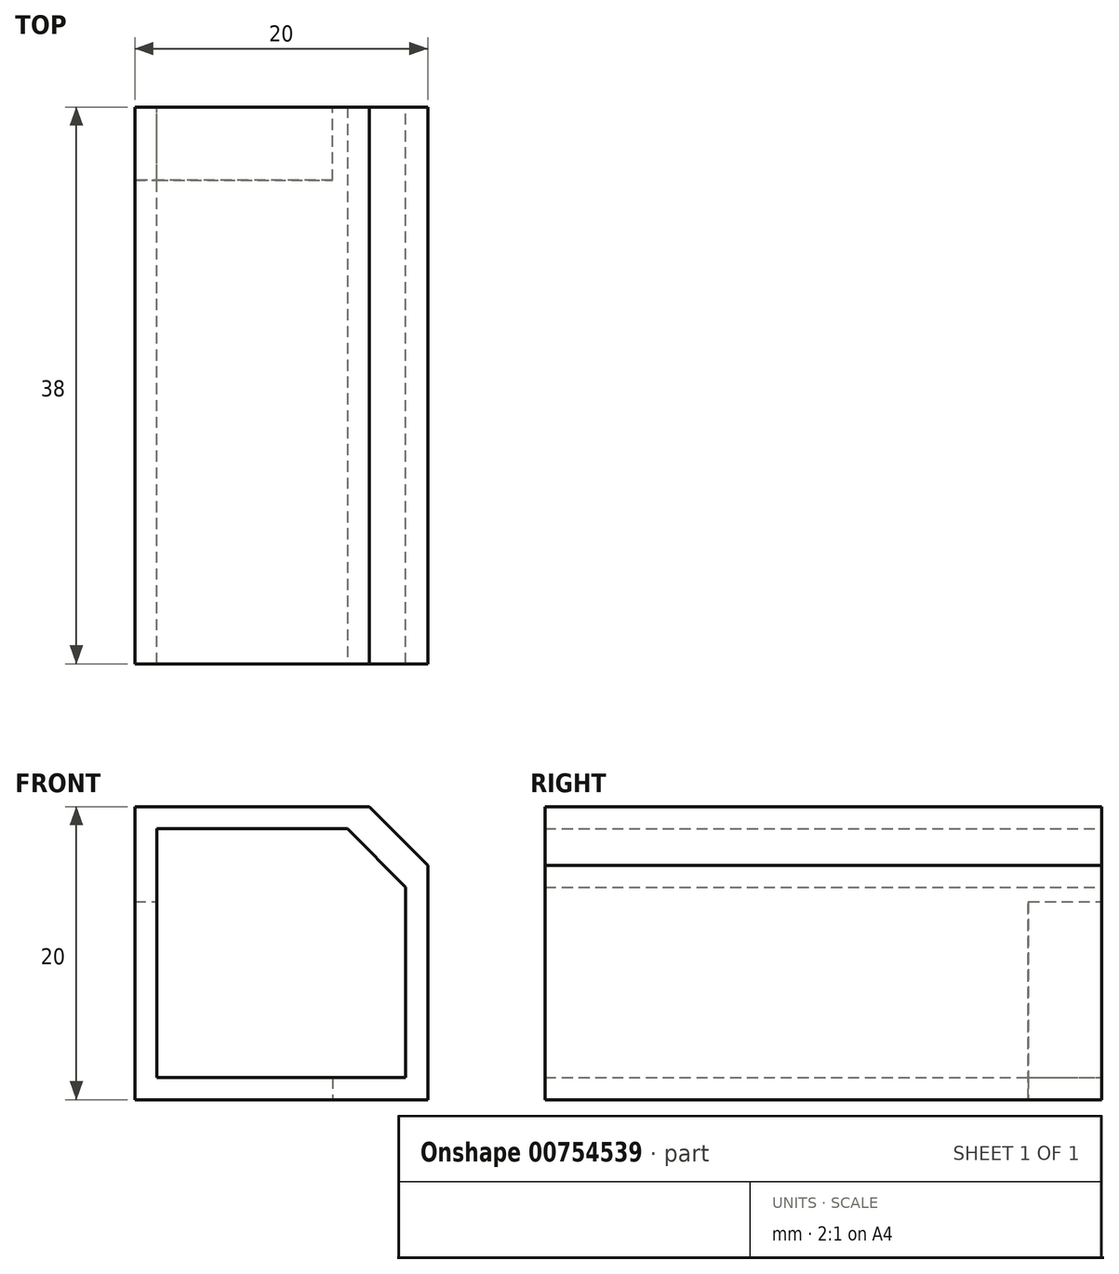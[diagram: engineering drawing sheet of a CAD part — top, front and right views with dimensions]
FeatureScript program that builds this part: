
annotation { "Feature Type Name" : "Feature", "Feature Type Description" : "" }
export const myFeature = defineFeature(function(context is Context, id is Id, definition is map)
    precondition{}
    {
        {
            var Q0;
            Q0=qCreatedBy(makeId("Front.planeOp"),FACE);
            var sketch = newSketch(context, id + "F0", { "sketchPlane" : qUnion([Q0])});
            skLineSegment(sketch, "E0.bottom", {"start": v(0, 0) * mm, "end": v(20, 0) * mm});
            skLineSegment(sketch, "E0.top", {"start": v(0, 20) * mm, "end": v(20, 20) * mm});
            skLineSegment(sketch, "E0.left", {"start": v(0, 0) * mm, "end": v(0, 20) * mm});
            skLineSegment(sketch, "E0.right", {"start": v(20, 0) * mm, "end": v(20, 20) * mm});
            skLineSegment(sketch, "E1.bottom", {"start": v(1.5, 18.5) * mm, "end": v(18.5, 18.5) * mm});
            skLineSegment(sketch, "E1.top", {"start": v(1.5, 1.5) * mm, "end": v(18.5, 1.5) * mm});
            skLineSegment(sketch, "E1.left", {"start": v(1.5, 18.5) * mm, "end": v(1.5, 1.5) * mm});
            skLineSegment(sketch, "E1.right", {"start": v(18.5, 18.5) * mm, "end": v(18.5, 1.5) * mm});
            skSolve(sketch);
        }
        {
            var Q0;
            Q0=makeQuery(id+"F0.imprint","IMPRINT",FACE,{"disambiguationData":[TD([[makeQuery(id+"F0.imprint","IMPRINT",EDGE,{"derivedFrom":sQuery(id+"F0.wireOp",EDGE,"E0.bottom")}),1.0]])]});
            extrude(context, id + "F1", {"entities" : qUnion([Q0]), "depth" : 38 * mm, "offsetDistance" : 25 * mm});
        }
        {
            var Q0;
            Q0=makeQuery(id+"F1.opExtrude","SWEPT_EDGE",EDGE,{"disambiguationData":[OSD([sQuery(id+"F0.wireOp",EDGE,"E0.top"),sQuery(id+"F0.wireOp",EDGE,"E0.right")])]});
            var Q1;
            Q1=makeQuery(id+"F1.opExtrude","SWEPT_EDGE",EDGE,{"disambiguationData":[OSD([sQuery(id+"F0.wireOp",EDGE,"E1.bottom"),sQuery(id+"F0.wireOp",EDGE,"E1.right")])]});
            chamfer(context, id + "F2", {"entities" : qUnion([Q0, Q1]), "width" : 4 * mm, "tangentPropagation" : true});
        }
        {
            var Q0;
            Q0=qCreatedBy(makeId("Front.planeOp"),FACE);
            var sketch = newSketch(context, id + "F3", { "sketchPlane" : qUnion([Q0])});
            skLineSegment(sketch, "E2", {"start": v(0, 0) * mm, "end": v(0, 13.5) * mm});
            skLineSegment(sketch, "E3", {"start": v(0, 13.5) * mm, "end": v(1.5, 13.5) * mm});
            skLineSegment(sketch, "E4", {"start": v(1.5, 13.5) * mm, "end": v(1.5, 1.5) * mm});
            skLineSegment(sketch, "E5", {"start": v(1.5, 1.5) * mm, "end": v(13.5, 1.5) * mm});
            skLineSegment(sketch, "E6", {"start": v(13.5, 1.5) * mm, "end": v(13.5, 0) * mm});
            skLineSegment(sketch, "E7", {"start": v(13.5, 0) * mm, "end": v(0, 0) * mm});
            skSolve(sketch);
        }
        {
            var Q0;
            Q0=makeQuery(id+"F1.opExtrude","CAP_FACE",FACE,{"disambiguationData":[OSD([sQuery(id+"F0.wireOp",EDGE,"E0.bottom"),sQuery(id+"F0.wireOp",EDGE,"E0.top"),sQuery(id+"F0.wireOp",EDGE,"E0.left"),sQuery(id+"F0.wireOp",EDGE,"E0.right"),sQuery(id+"F0.wireOp",EDGE,"E1.bottom"),sQuery(id+"F0.wireOp",EDGE,"E1.top"),sQuery(id+"F0.wireOp",EDGE,"E1.left"),sQuery(id+"F0.wireOp",EDGE,"E1.right")])],"isStart":false});
            var Q1;
            Q1=makeQuery(id+"F3.imprint","IMPRINT",FACE,{"disambiguationData":[TD([[makeQuery(id+"F3.imprint","IMPRINT",EDGE,{"derivedFrom":sQuery(id+"F3.wireOp",EDGE,"E2")}),-1.0]])]});
            extrude(context, id + "F4", {"entities" : qUnion([Q0, Q1]), "operationType" : NewBodyOperationType.REMOVE, "depth" : 5 * mm, "offsetDistance" : 25 * mm});
        }
    });
